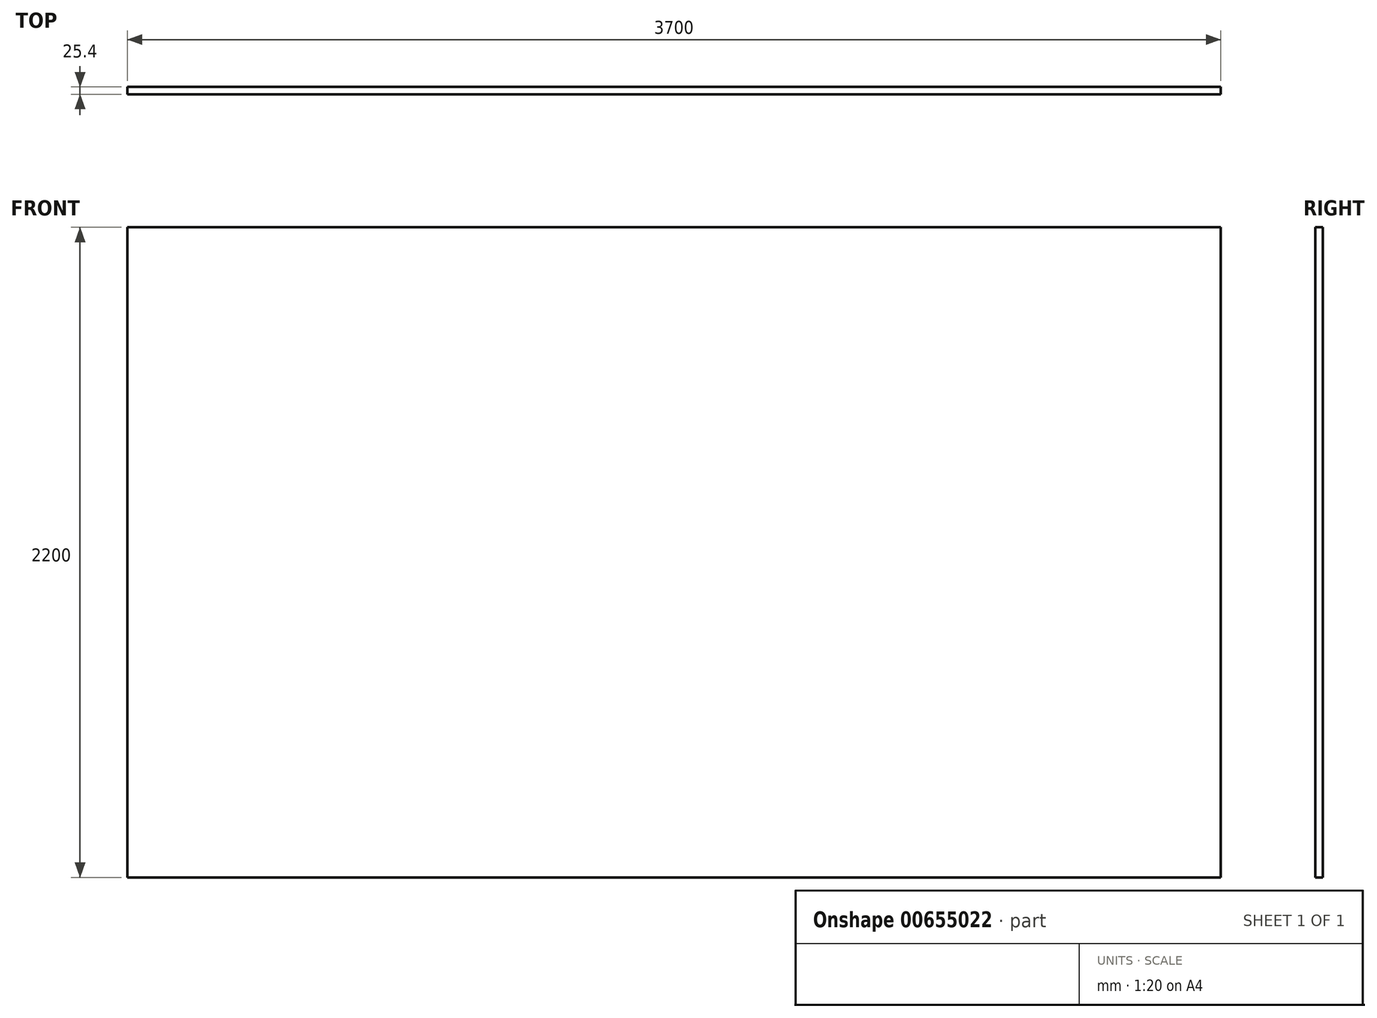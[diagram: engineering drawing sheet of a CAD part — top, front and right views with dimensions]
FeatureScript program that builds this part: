
annotation { "Feature Type Name" : "Feature", "Feature Type Description" : "" }
export const myFeature = defineFeature(function(context is Context, id is Id, definition is map)
    precondition{}
    {
        {
            var Q0;
            Q0=qCreatedBy(makeId("Front.planeOp"),FACE);
            var sketch = newSketch(context, id + "F0", { "sketchPlane" : qUnion([Q0])});
            skLineSegment(sketch, "E0.bottom", {"start": v(1850, -1100) * mm, "end": v(-1850, -1100) * mm});
            skLineSegment(sketch, "E0.top", {"start": v(1850, 1100) * mm, "end": v(-1850, 1100) * mm});
            skLineSegment(sketch, "E0.left", {"start": v(1850, -1100) * mm, "end": v(1850, 1100) * mm});
            skLineSegment(sketch, "E0.right", {"start": v(-1850, -1100) * mm, "end": v(-1850, 1100) * mm});
            skPoint(sketch, "E0.middle", {"position": v(0, 0) * mm});
            skSolve(sketch);
        }
        {
            var Q0;
            Q0 = qSketchRegion(id + "F0", true);
            extrude(context, id + "F1", {"entities" : qUnion([Q0]), "depth" : 25.4 * mm, "offsetDistance" : 25.4 * mm});
        }
    });
